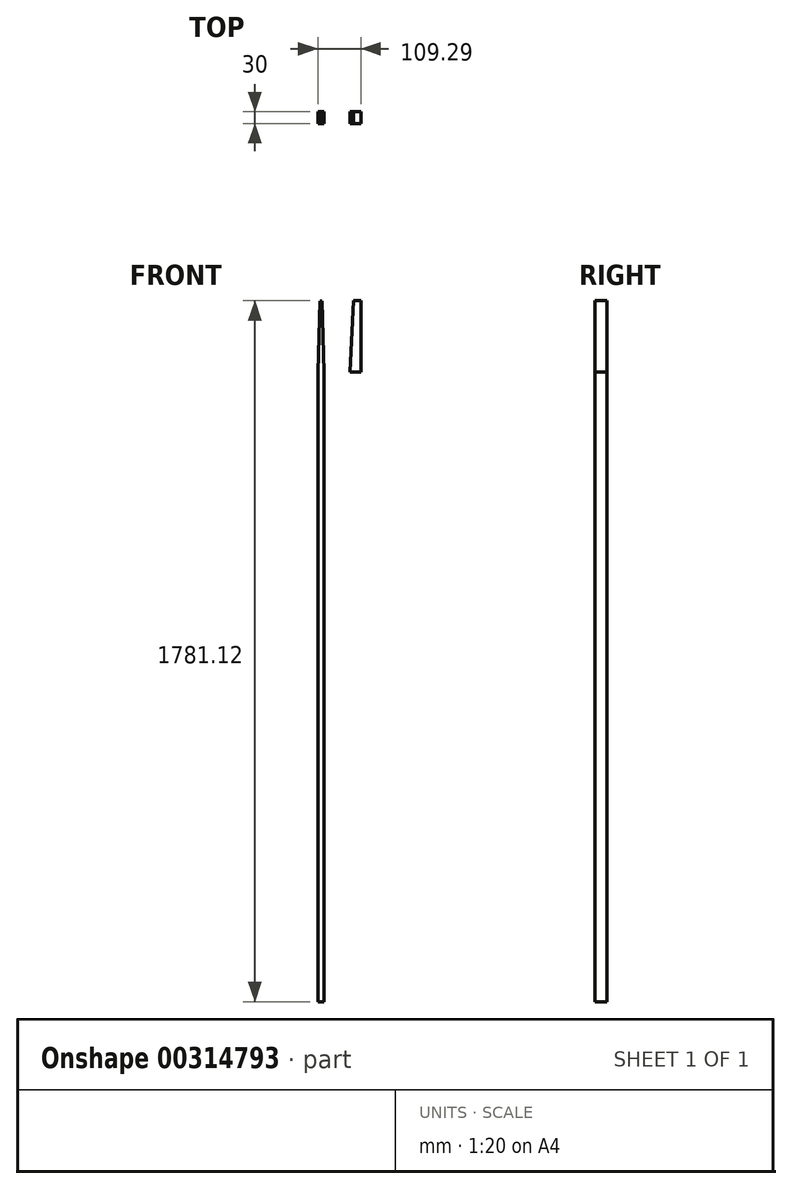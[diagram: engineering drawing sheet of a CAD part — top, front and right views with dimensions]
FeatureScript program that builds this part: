
annotation { "Feature Type Name" : "Feature", "Feature Type Description" : "" }
export const myFeature = defineFeature(function(context is Context, id is Id, definition is map)
    precondition{}
    {
        {
            var Q0;
            Q0=qCreatedBy(makeId("Front.planeOp"),FACE);
            var sketch = newSketch(context, id + "F0", { "sketchPlane" : qUnion([Q0])});
            skLineSegment(sketch, "E0", {"start": v(0, 0) * mm, "end": v(0, 180) * mm});
            skLineSegment(sketch, "E1", {"start": v(0, 0) * mm, "end": v(7.5, 0) * mm});
            skLineSegment(sketch, "E2", {"start": v(7.5, 0) * mm, "end": v(2.5, 180) * mm});
            skLineSegment(sketch, "E3", {"start": v(2.5, 180) * mm, "end": v(0, 180) * mm});
            skLineSegment(sketch, "E4", {"start": v(0, 0) * mm, "end": v(-7.5, 0) * mm});
            skLineSegment(sketch, "E5", {"start": v(-7.5, 0) * mm, "end": v(-2.5, 180.02) * mm});
            skLineSegment(sketch, "E6", {"start": v(-2.5, 180.02) * mm, "end": v(0, 180) * mm});
            skLineSegment(sketch, "E7.bottom", {"start": v(-7.5, 0) * mm, "end": v(7.5, 0) * mm});
            skLineSegment(sketch, "E7.top", {"start": v(-7.5, -1600) * mm, "end": v(7.5, -1600) * mm});
            skLineSegment(sketch, "E7.left", {"start": v(-7.5, 0) * mm, "end": v(-7.5, -1600) * mm});
            skLineSegment(sketch, "E7.right", {"start": v(7.5, 0) * mm, "end": v(7.5, -1600) * mm});
            skSolve(sketch);
        }
        {
            var Q0;
            Q0 = qSketchRegion(id + "F0", true);
            extrude(context, id + "F1", {"entities" : qUnion([Q0]), "depth" : 30 * mm});
        }
        {
            var Q0;
            Q0=qCreatedBy(makeId("Front.planeOp"),FACE);
            var sketch = newSketch(context, id + "F2", { "sketchPlane" : qUnion([Q0])});
            skLineSegment(sketch, "E8", {"start": v(74.43, 0) * mm, "end": v(82.85, 181.12) * mm});
            skLineSegment(sketch, "E9", {"start": v(82.85, 181.12) * mm, "end": v(101.8, 181.12) * mm});
            skLineSegment(sketch, "E10", {"start": v(101.8, 181.12) * mm, "end": v(101.8, 184.8) * mm});
            skLineSegment(sketch, "E11", {"start": v(101.8, 184.8) * mm, "end": v(101.8, 0) * mm});
            skLineSegment(sketch, "E12", {"start": v(74.43, 0) * mm, "end": v(101.8, 0) * mm});
            skSolve(sketch);
        }
        {
            var Q0;
            Q0 = qSketchRegion(id + "F2", true);
            extrude(context, id + "F3", {"entities" : qUnion([Q0]), "depth" : 30 * mm});
        }
    });
